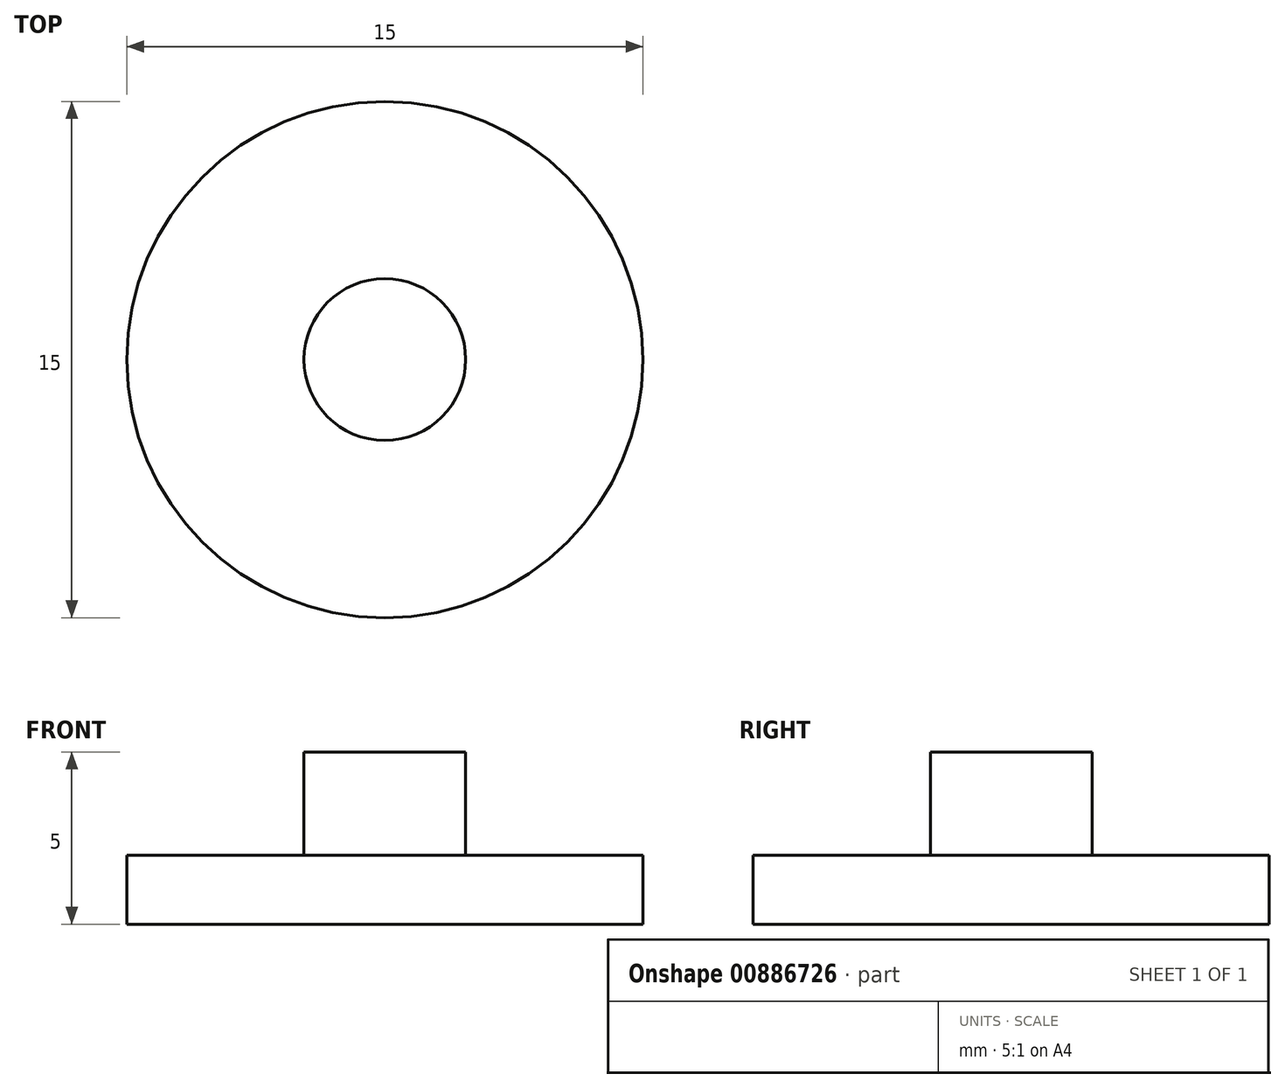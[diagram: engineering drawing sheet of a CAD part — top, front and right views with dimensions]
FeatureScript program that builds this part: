
annotation { "Feature Type Name" : "Feature", "Feature Type Description" : "" }
export const myFeature = defineFeature(function(context is Context, id is Id, definition is map)
    precondition{}
    {
        {
            var Q0;
            Q0=qCreatedBy(makeId("Top.planeOp"),FACE);
            var sketch = newSketch(context, id + "F0", { "sketchPlane" : qUnion([Q0])});
            skCircle(sketch, "E0", {"center": v(-37.07, 46.7) * mm, "radius": 7.5 * mm});
            skSolve(sketch);
        }
        {
            var Q0;
            Q0=makeQuery(id+"F0.imprint","IMPRINT",FACE,{"disambiguationData":[TD([[makeQuery(id+"F0.imprint","IMPRINT",EDGE,{"derivedFrom":sQuery(id+"F0.wireOp",EDGE,"FHHY5vHs-BrvE-mJzX-BjVy-1mGiXT1TOY0g")}),1.0]])]});
            var Q1;
            Q1=makeQuery(id+"F0.imprint","IMPRINT",FACE,{"disambiguationData":[TD([[makeQuery(id+"F0.imprint","IMPRINT",EDGE,{"derivedFrom":sQuery(id+"F0.wireOp",EDGE,"E0")}),1.0]])]});
            var Q2;
            Q2 = qSketchRegion(id + "F2", true);
            extrude(context, id + "F1", {"entities" : qUnion([Q0, Q1, Q2]), "depth" : 2 * mm, "offsetDistance" : 25.4 * mm});
        }
        {
            var Q0;
            Q0=makeQuery(id+"F1.opExtrude","CAP_FACE",FACE,{"disambiguationData":[OSD([sQuery(id+"F0.wireOp",EDGE,"E0")])],"isStart":false});
            var sketch = newSketch(context, id + "F2", { "sketchPlane" : qUnion([Q0])});
            skCircle(sketch, "E1", {"center": v(-37.07, 46.7) * mm, "radius": 2.35 * mm});
            skSolve(sketch);
        }
        {
            var Q0;
            Q0 = qSketchRegion(id + "F2", true);
            extrude(context, id + "F3", {"entities" : qUnion([Q0]), "operationType" : NewBodyOperationType.ADD, "depth" : 3 * mm, "offsetDistance" : 25.4 * mm});
        }
    });
